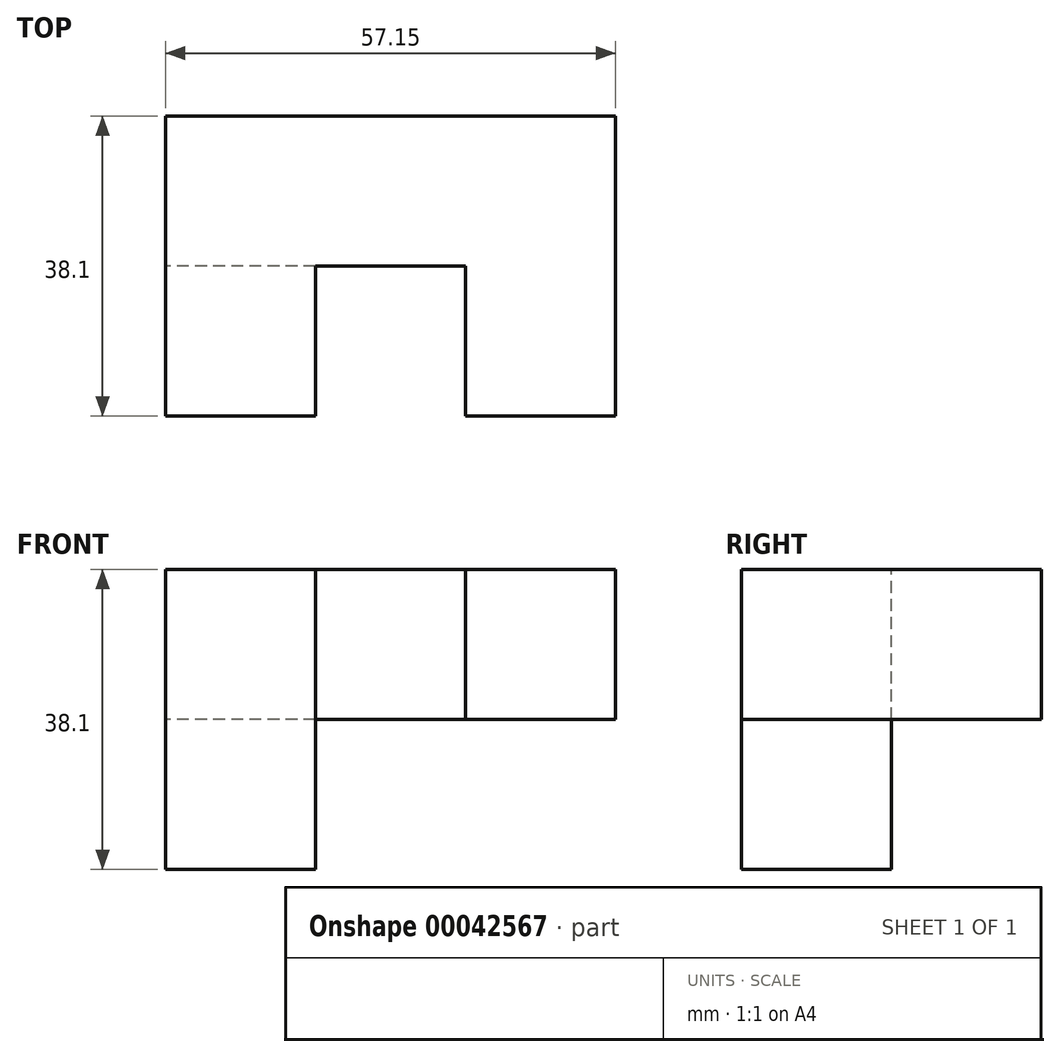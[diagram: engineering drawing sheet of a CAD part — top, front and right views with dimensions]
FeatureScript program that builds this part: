
annotation { "Feature Type Name" : "Feature", "Feature Type Description" : "" }
export const myFeature = defineFeature(function(context is Context, id is Id, definition is map)
    precondition{}
    {
        {
            var Q0;
            Q0=qCreatedBy(makeId("Top.planeOp"),FACE);
            var sketch = newSketch(context, id + "F0", { "sketchPlane" : qUnion([Q0])});
            skLineSegment(sketch, "E0.bottom", {"start": v(0, 0) * mm, "end": v(-19.05, 0) * mm});
            skLineSegment(sketch, "E0.top", {"start": v(0, 19.05) * mm, "end": v(-19.05, 19.05) * mm});
            skLineSegment(sketch, "E0.left", {"start": v(0, 0) * mm, "end": v(0, 19.05) * mm});
            skLineSegment(sketch, "E0.right", {"start": v(-19.05, 0) * mm, "end": v(-19.05, 19.05) * mm});
            skSolve(sketch);
        }
        {
            var Q0;
            Q0=makeQuery(id+"F0.imprint","IMPRINT",FACE,{"disambiguationData":[TD([[makeQuery(id+"F0.imprint","IMPRINT",EDGE,{"derivedFrom":sQuery(id+"F0.wireOp",EDGE,"E0.bottom")}),-1.0]])]});
            extrude(context, id + "F1", {"entities" : qUnion([Q0]), "depth" : 38.1 * mm});
        }
        {
            var Q0;
            Q0=makeQuery(id+"F1.opExtrude","SWEPT_FACE",FACE,{"disambiguationData":[OSD([sQuery(id+"F0.wireOp",EDGE,"E0.top")])]});
            var sketch = newSketch(context, id + "F2", { "sketchPlane" : qUnion([Q0])});
            skLineSegment(sketch, "E1.bottom", {"start": v(0, 38.1) * mm, "end": v(19.05, 38.1) * mm});
            skLineSegment(sketch, "E1.top", {"start": v(0, 19.05) * mm, "end": v(19.05, 19.05) * mm});
            skLineSegment(sketch, "E1.left", {"start": v(0, 38.1) * mm, "end": v(0, 19.05) * mm});
            skLineSegment(sketch, "E1.right", {"start": v(19.05, 38.1) * mm, "end": v(19.05, 19.05) * mm});
            skSolve(sketch);
        }
        {
            var Q0;
            Q0=makeQuery(id+"F2.imprint","IMPRINT",FACE,{"disambiguationData":[TD([[makeQuery(id+"F2.imprint","IMPRINT",EDGE,{"derivedFrom":sQuery(id+"F2.wireOp",EDGE,"E1.bottom")}),-1.0]])]});
            extrude(context, id + "F3", {"entities" : qUnion([Q0]), "operationType" : NewBodyOperationType.ADD, "depth" : 19.05 * mm});
        }
        {
            var Q0;
            Q0=makeQuery(id+"F3.boolean.opBoolean","MERGE",FACE,{"derivedFrom":[makeQuery(id+"F1.opExtrude","SWEPT_FACE",FACE,{"disambiguationData":[OSD([sQuery(id+"F0.wireOp",EDGE,"E0.left")])]}),makeQuery(id+"F3.opExtrude","SWEPT_FACE",FACE,{"disambiguationData":[OSD([sQuery(id+"F2.wireOp",EDGE,"E1.left")])]})]});
            var sketch = newSketch(context, id + "F4", { "sketchPlane" : qUnion([Q0])});
            skLineSegment(sketch, "E2.bottom", {"start": v(38.1, 19.05) * mm, "end": v(19.05, 19.05) * mm});
            skLineSegment(sketch, "E2.top", {"start": v(38.1, 38.1) * mm, "end": v(19.05, 38.1) * mm});
            skLineSegment(sketch, "E2.left", {"start": v(38.1, 19.05) * mm, "end": v(38.1, 38.1) * mm});
            skLineSegment(sketch, "E2.right", {"start": v(19.05, 19.05) * mm, "end": v(19.05, 38.1) * mm});
            skSolve(sketch);
        }
        {
            var Q0;
            Q0=makeQuery(id+"F4.imprint","IMPRINT",FACE,{"disambiguationData":[TD([[makeQuery(id+"F4.imprint","IMPRINT",EDGE,{"derivedFrom":sQuery(id+"F4.wireOp",EDGE,"E2.bottom")}),-1.0]])]});
            extrude(context, id + "F5", {"entities" : qUnion([Q0]), "operationType" : NewBodyOperationType.ADD, "depth" : 38.1 * mm});
        }
        {
            var Q0;
            Q0=makeQuery(id+"F5.opExtrude","SWEPT_FACE",FACE,{"disambiguationData":[OSD([sQuery(id+"F4.wireOp",EDGE,"E2.right")])]});
            var sketch = newSketch(context, id + "F6", { "sketchPlane" : qUnion([Q0])});
            skLineSegment(sketch, "E3.bottom", {"start": v(38.1, 19.05) * mm, "end": v(19.05, 19.05) * mm});
            skLineSegment(sketch, "E3.top", {"start": v(38.1, 38.1) * mm, "end": v(19.05, 38.1) * mm});
            skLineSegment(sketch, "E3.left", {"start": v(38.1, 19.05) * mm, "end": v(38.1, 38.1) * mm});
            skLineSegment(sketch, "E3.right", {"start": v(19.05, 19.05) * mm, "end": v(19.05, 38.1) * mm});
            skSolve(sketch);
        }
        {
            var Q0;
            Q0=makeQuery(id+"F6.imprint","IMPRINT",FACE,{"disambiguationData":[TD([[makeQuery(id+"F6.imprint","IMPRINT",EDGE,{"derivedFrom":sQuery(id+"F6.wireOp",EDGE,"E3.bottom")}),-1.0]])]});
            extrude(context, id + "F7", {"entities" : qUnion([Q0]), "operationType" : NewBodyOperationType.ADD, "depth" : 19.05 * mm});
        }
    });
